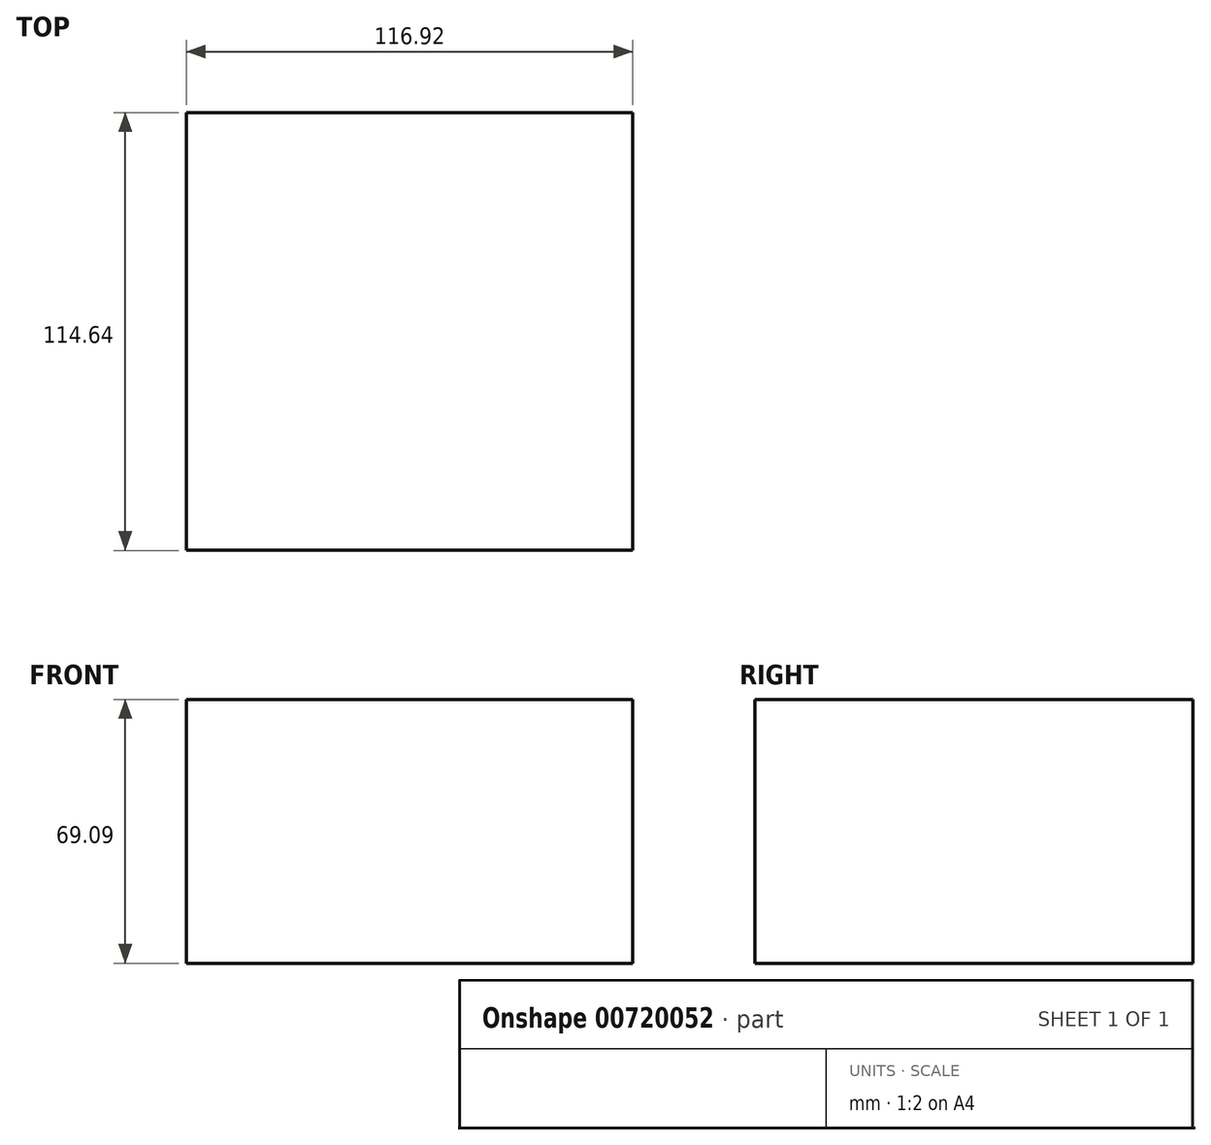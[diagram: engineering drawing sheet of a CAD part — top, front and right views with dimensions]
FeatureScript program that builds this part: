
annotation { "Feature Type Name" : "Feature", "Feature Type Description" : "" }
export const myFeature = defineFeature(function(context is Context, id is Id, definition is map)
    precondition{}
    {
        {
            var Q0;
            Q0=qCreatedBy(makeId("Top.planeOp"),FACE);
            var sketch = newSketch(context, id + "F0", { "sketchPlane" : qUnion([Q0])});
            skLineSegment(sketch, "E0.bottom", {"start": v(-58.27, 56.56) * mm, "end": v(58.65, 56.56) * mm});
            skLineSegment(sketch, "E0.top", {"start": v(-58.27, -58.08) * mm, "end": v(58.65, -58.08) * mm});
            skLineSegment(sketch, "E0.left", {"start": v(-58.27, 56.56) * mm, "end": v(-58.27, -58.08) * mm});
            skLineSegment(sketch, "E0.right", {"start": v(58.65, 56.56) * mm, "end": v(58.65, -58.08) * mm});
            skSolve(sketch);
        }
        {
            var Q0;
            Q0=makeQuery(id+"F0.imprint","IMPRINT",FACE,{"disambiguationData":[TD([[makeQuery(id+"F0.imprint","IMPRINT",EDGE,{"derivedFrom":sQuery(id+"F0.wireOp",EDGE,"E0.bottom")}),-1.0]])]});
            extrude(context, id + "F1", {"entities" : qUnion([Q0]), "depth" : 69.1 * mm, "offsetDistance" : 25.4 * mm});
        }
    });
